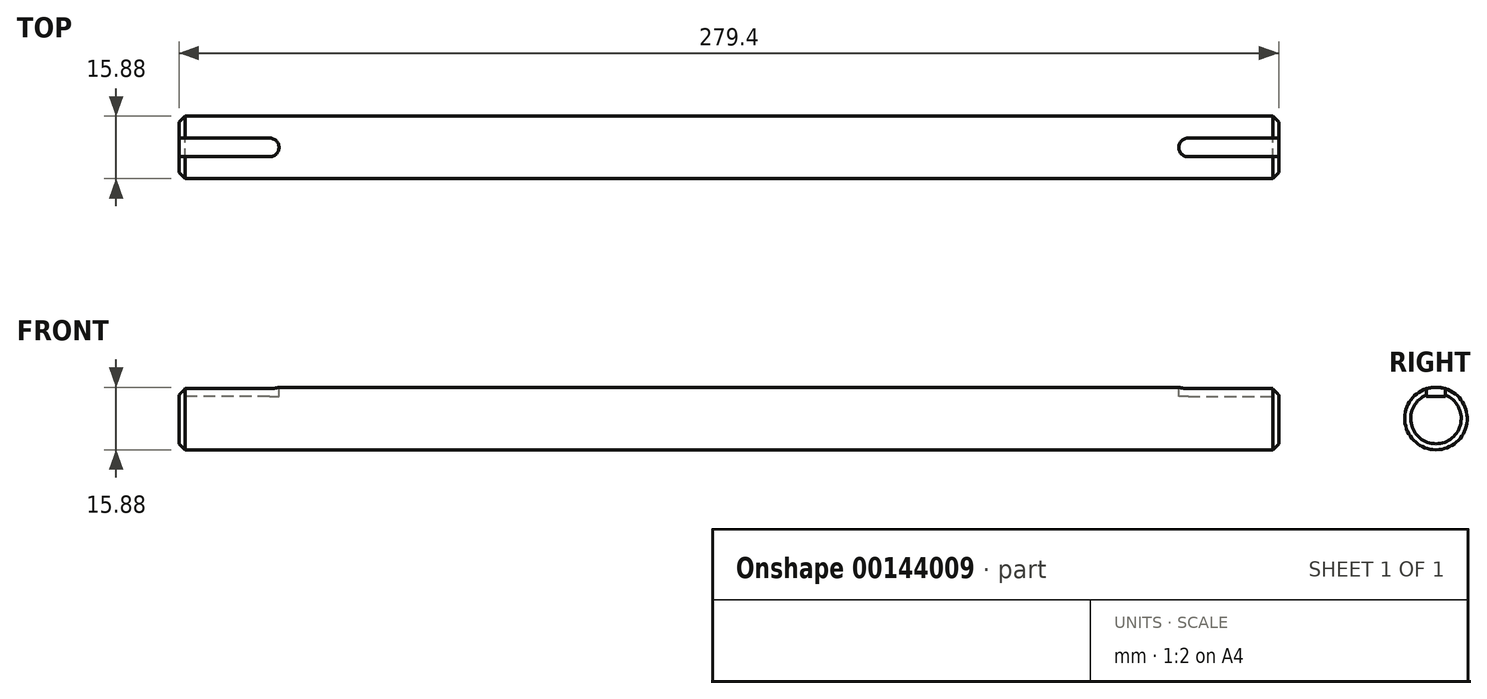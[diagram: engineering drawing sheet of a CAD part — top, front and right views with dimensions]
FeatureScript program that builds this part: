
annotation { "Feature Type Name" : "Feature", "Feature Type Description" : "" }
export const myFeature = defineFeature(function(context is Context, id is Id, definition is map)
    precondition{}
    {
        {
            var Q0;
            Q0=qCreatedBy(makeId("Right.planeOp"),FACE);
            var sketch = newSketch(context, id + "F0", { "sketchPlane" : qUnion([Q0])});
            skCircle(sketch, "E0", {"center": v(0, 0) * mm, "radius": 7.94 * mm});
            skSolve(sketch);
        }
        {
            var Q0;
            Q0=qSketchRegion(id+"F0",true);
            extrude(context, id + "F1", {"entities" : qUnion([Q0]), "endBound" : BoundingType.SYMMETRIC, "depth" : 279.4 * mm});
        }
        {
            var Q0;
            Q0=qCreatedBy(makeId("Top.planeOp"),FACE);
            cPlane(context, id + "F2", {"entities" : qUnion([Q0]), "cplaneType" : CPlaneType.OFFSET, "offset" : 7.94 * mm, "width" : 152.4 * mm, "height" : 152.4 * mm});
        }
        {
            var Q0;
            Q0=qCreatedBy(id+"F2.planeOp",FACE);
            var sketch = newSketch(context, id + "F3", { "sketchPlane" : qUnion([Q0])});
            skLineSegment(sketch, "E1.0", {"start": v(-139.7, 7.94) * mm, "end": v(-139.7, -7.94) * mm, "construction": true});
            skLineSegment(sketch, "E2.0", {"start": v(139.7, 7.94) * mm, "end": v(139.7, -7.94) * mm, "construction": true});
            skLineSegment(sketch, "E3", {"start": v(-139.7, 0) * mm, "end": v(139.7, 0) * mm, "construction": true});
            skLineSegment(sketch, "E4.0", {"start": v(-116.69, 7.94) * mm, "end": v(-116.69, -7.94) * mm, "construction": true});
            skCircle(sketch, "E5", {"center": v(-116.69, 0) * mm, "radius": 2.38 * mm});
            skLineSegment(sketch, "E6", {"start": v(-116.69, -2.38) * mm, "end": v(-141.9, -2.38) * mm});
            skLineSegment(sketch, "E7", {"start": v(-116.69, 2.38) * mm, "end": v(-143.45, 2.38) * mm});
            skLineSegment(sketch, "E8", {"start": v(-139.7, 2.38) * mm, "end": v(-139.7, -2.38) * mm});
            skLineSegment(sketch, "E9", {"start": v(139.7, -7.94) * mm, "end": v(-139.7, -7.94) * mm, "construction": true});
            skLineSegment(sketch, "E10", {"start": v(0, 29.74) * mm, "end": v(0, -35.72) * mm, "construction": true});
            skPoint(sketch, "E10.startSnap0", {"position": v(0, 0) * mm});
            skCircle(sketch, "E11.MirrorC", {"center": v(116.69, 0) * mm, "radius": 2.38 * mm});
            skLineSegment(sketch, "E12.MirrorCS", {"start": v(139.7, 2.38) * mm, "end": v(139.7, -2.38) * mm});
            skLineSegment(sketch, "E13.MirrorCS", {"start": v(139.7, 7.94) * mm, "end": v(139.7, -7.94) * mm});
            skLineSegment(sketch, "E14.MirrorCS", {"start": v(116.69, 7.94) * mm, "end": v(116.69, -7.94) * mm});
            skLineSegment(sketch, "E15.MirrorCS", {"start": v(116.69, 2.38) * mm, "end": v(143.45, 2.38) * mm});
            skLineSegment(sketch, "E16.MirrorCS", {"start": v(116.69, -2.38) * mm, "end": v(141.9, -2.38) * mm});
            skSolve(sketch);
        }
        {
            var Q0;
            Q0=qSketchRegion(id+"F3",true);
            extrude(context, id + "F4", {"entities" : qUnion([Q0]), "operationType" : NewBodyOperationType.REMOVE, "oppositeDirection" : true, "depth" : 2.38 * mm});
        }
        {
            var Q0;
            Q0=makeQuery(id+"F1.opExtrude","CAP_EDGE",EDGE,{"disambiguationData":[OSD([sQuery(id+"F0.wireOp",EDGE,"E0")])],"isStart":true});
            var Q1;
            Q1=makeQuery(id+"F1.opExtrude","CAP_EDGE",EDGE,{"disambiguationData":[OSD([sQuery(id+"F0.wireOp",EDGE,"E0")])],"isStart":false});
            chamfer(context, id + "F5", {"entities" : qUnion([Q0, Q1]), "width" : 1.52 * mm, "tangentPropagation" : true});
        }
    });
